# Revit family: Einbaugeräte_Modul_45-Systeme_Steckdose_33°_Schutzkontakt_3_fach
name_source: partatom
category: Generic Models
revit_build: Autodesk Revit 2015 (Build: 20140606_1530(x64)
units: mm (PartAtom-declared; Revit-internal decimal feet)

## types (6) — shared parameters
Manufacturer = OBO Bettermann
URL = http://www.obo-bettermann.com

## per-type parameters (varying)
| type | GTIN | Manufacturer Art. No. | Material |
| STD-D3 MZGN3 | 4012196047925 | 6120126 | Polycarbonate, minzgrün |
| STD-D3 ROR3 | 4012196047871 | 6120124 | Polycarbonate, reinorange |
| STD-D3 RW3 | 4012196047864 | 6120122 | Polycarbonate, Clear reinweiß |
| STD-D3 SRO3 | 4012196047949 | 6120128 | Polycarbonate, signalrot |
| STD-D3 AL3 | 4012196047994 | 6120132 | Polycarbonate,Alu lackiert |
| STD-D3 SWGR3 | 4012196047987 | 6120130 | Polycarbonate, schwarzgrau |

note: column(s) folded — value = type name in every type: Article Type

## geometry (parser evidence)
native form markers: Sweep x2
no freeform markers — native parametric forms only
